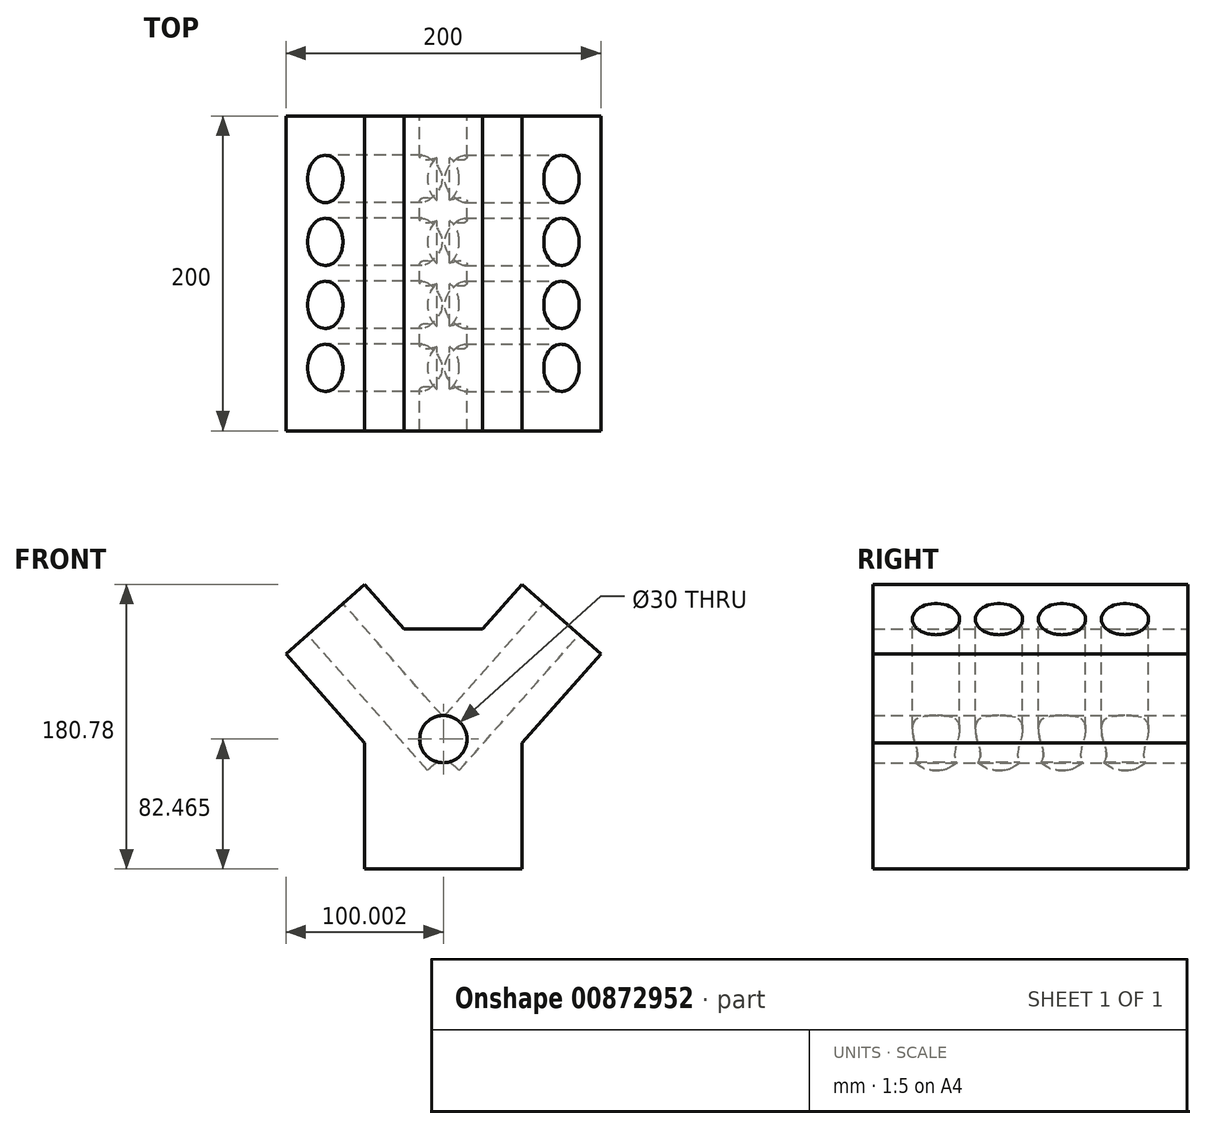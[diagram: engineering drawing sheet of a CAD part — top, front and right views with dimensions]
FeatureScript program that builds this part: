
annotation { "Feature Type Name" : "Feature", "Feature Type Description" : "" }
export const myFeature = defineFeature(function(context is Context, id is Id, definition is map)
    precondition{}
    {
        {
            var Q0;
            Q0=qCreatedBy(makeId("Front.planeOp"),FACE);
            var sketch = newSketch(context, id + "F0", { "sketchPlane" : qUnion([Q0])});
            skLineSegment(sketch, "E0.bottom", {"start": v(-63.95, -46.12) * mm, "end": v(-13.95, -46.12) * mm});
            skLineSegment(sketch, "E0.left", {"start": v(-63.95, -46.12) * mm, "end": v(-63.95, 33.88) * mm});
            skLineSegment(sketch, "E1", {"start": v(-63.95, 33.88) * mm, "end": v(-113.95, 90.51) * mm});
            skLineSegment(sketch, "E2", {"start": v(-113.95, 90.51) * mm, "end": v(-63.95, 134.66) * mm});
            skLineSegment(sketch, "E3", {"start": v(-63.95, 134.66) * mm, "end": v(-38.95, 106.34) * mm});
            skLineSegment(sketch, "E4", {"start": v(-38.95, 106.34) * mm, "end": v(-13.95, 106.34) * mm});
            skLineSegment(sketch, "E5.MirrorCS", {"start": v(11.05, 106.34) * mm, "end": v(-22.8, 106.34) * mm});
            skLineSegment(sketch, "E6.MirrorCS", {"start": v(86.05, 90.51) * mm, "end": v(36.05, 134.66) * mm});
            skLineSegment(sketch, "E7.MirrorCS", {"start": v(36.05, -46.12) * mm, "end": v(36.05, 33.88) * mm});
            skLineSegment(sketch, "E8.MirrorCS", {"start": v(36.05, -46.12) * mm, "end": v(-13.95, -46.12) * mm});
            skLineSegment(sketch, "E9.MirrorCS", {"start": v(36.05, 33.88) * mm, "end": v(86.05, 90.51) * mm});
            skLineSegment(sketch, "E10.MirrorCS", {"start": v(36.05, 134.66) * mm, "end": v(11.05, 106.34) * mm});
            skCircle(sketch, "E11", {"center": v(-13.95, 36.34) * mm, "radius": 15 * mm});
            skSolve(sketch);
        }
        {
            var Q0;
            Q0=makeQuery(id+"F0.imprint","IMPRINT",FACE,{"disambiguationData":[TD([[makeQuery(id+"F0.imprint","IMPRINT",EDGE,{"derivedFrom":sQuery(id+"F0.wireOp",EDGE,"E0.bottom")}),1.0]])]});
            extrude(context, id + "F1", {"entities" : qUnion([Q0]), "depth" : 200 * mm, "offsetDistance" : 25 * mm});
        }
        {
            var Q0;
            Q0=makeQuery(id+"F1.opExtrude","SWEPT_FACE",FACE,{"disambiguationData":[OSD([sQuery(id+"F0.wireOp",EDGE,"E2")])]});
            var sketch = newSketch(context, id + "F2", { "sketchPlane" : qUnion([Q0])});
            skPoint(sketch, "E12", {"position": v(7.84, -40) * mm});
            skPoint(sketch, "E13", {"position": v(7.84, -80) * mm});
            skPoint(sketch, "E14", {"position": v(7.84, -120) * mm});
            skPoint(sketch, "E15", {"position": v(7.84, -160) * mm});
            skCircle(sketch, "E16", {"center": v(7.84, -40) * mm, "radius": 15 * mm});
            skCircle(sketch, "E17", {"center": v(7.84, -80) * mm, "radius": 15 * mm});
            skCircle(sketch, "E18", {"center": v(7.84, -120) * mm, "radius": 15 * mm});
            skCircle(sketch, "E19", {"center": v(7.84, -160) * mm, "radius": 15 * mm});
            skSolve(sketch);
        }
        {
            var Q0;
            Q0=makeQuery(id+"F2.imprint","IMPRINT",FACE,{"disambiguationData":[TD([[makeQuery(id+"F2.imprint","IMPRINT",EDGE,{"derivedFrom":sQuery(id+"F2.wireOp",EDGE,"E16")}),1.0]])]});
            var Q1;
            Q1=makeQuery(id+"F2.imprint","IMPRINT",FACE,{"disambiguationData":[TD([[makeQuery(id+"F2.imprint","IMPRINT",EDGE,{"derivedFrom":sQuery(id+"F2.wireOp",EDGE,"E17")}),1.0]])]});
            var Q2;
            Q2=makeQuery(id+"F2.imprint","IMPRINT",FACE,{"disambiguationData":[TD([[makeQuery(id+"F2.imprint","IMPRINT",EDGE,{"derivedFrom":sQuery(id+"F2.wireOp",EDGE,"E19")}),1.0]])]});
            var Q3;
            Q3=makeQuery(id+"F2.imprint","IMPRINT",FACE,{"disambiguationData":[TD([[makeQuery(id+"F2.imprint","IMPRINT",EDGE,{"derivedFrom":sQuery(id+"F2.wireOp",EDGE,"E18")}),1.0]])]});
            extrude(context, id + "F3", {"entities" : qUnion([Q0, Q1, Q2, Q3]), "operationType" : NewBodyOperationType.REMOVE, "oppositeDirection" : true, "depth" : 115 * mm, "offsetDistance" : 25 * mm});
        }
        {
            var Q0;
            Q0=makeQuery(id+"F1.opExtrude","SWEPT_FACE",FACE,{"disambiguationData":[OSD([sQuery(id+"F0.wireOp",EDGE,"E6.MirrorCS")])]});
            var sketch = newSketch(context, id + "F4", { "sketchPlane" : qUnion([Q0])});
            skPoint(sketch, "E20", {"position": v(-28.75, -40) * mm});
            skPoint(sketch, "E21", {"position": v(-28.75, -80) * mm});
            skPoint(sketch, "E22", {"position": v(-28.75, -120) * mm});
            skPoint(sketch, "E23", {"position": v(-28.75, -160) * mm});
            skCircle(sketch, "E24", {"center": v(-28.75, -40) * mm, "radius": 15 * mm});
            skCircle(sketch, "E25", {"center": v(-28.75, -80) * mm, "radius": 15 * mm});
            skCircle(sketch, "E26", {"center": v(-28.75, -120) * mm, "radius": 15 * mm});
            skCircle(sketch, "E27", {"center": v(-28.75, -160) * mm, "radius": 15 * mm});
            skSolve(sketch);
        }
        {
            var Q0;
            Q0=makeQuery(id+"F4.imprint","IMPRINT",FACE,{"disambiguationData":[TD([[makeQuery(id+"F4.imprint","IMPRINT",EDGE,{"derivedFrom":sQuery(id+"F4.wireOp",EDGE,"E27")}),1.0]])]});
            var Q1;
            Q1=makeQuery(id+"F4.imprint","IMPRINT",FACE,{"disambiguationData":[TD([[makeQuery(id+"F4.imprint","IMPRINT",EDGE,{"derivedFrom":sQuery(id+"F4.wireOp",EDGE,"E26")}),1.0]])]});
            var Q2;
            Q2=makeQuery(id+"F4.imprint","IMPRINT",FACE,{"disambiguationData":[TD([[makeQuery(id+"F4.imprint","IMPRINT",EDGE,{"derivedFrom":sQuery(id+"F4.wireOp",EDGE,"E25")}),1.0]])]});
            var Q3;
            Q3=makeQuery(id+"F4.imprint","IMPRINT",FACE,{"disambiguationData":[TD([[makeQuery(id+"F4.imprint","IMPRINT",EDGE,{"derivedFrom":sQuery(id+"F4.wireOp",EDGE,"E24")}),1.0]])]});
            extrude(context, id + "F5", {"entities" : qUnion([Q0, Q1, Q2, Q3]), "operationType" : NewBodyOperationType.REMOVE, "oppositeDirection" : true, "depth" : 115 * mm, "offsetDistance" : 25 * mm});
        }
    });
